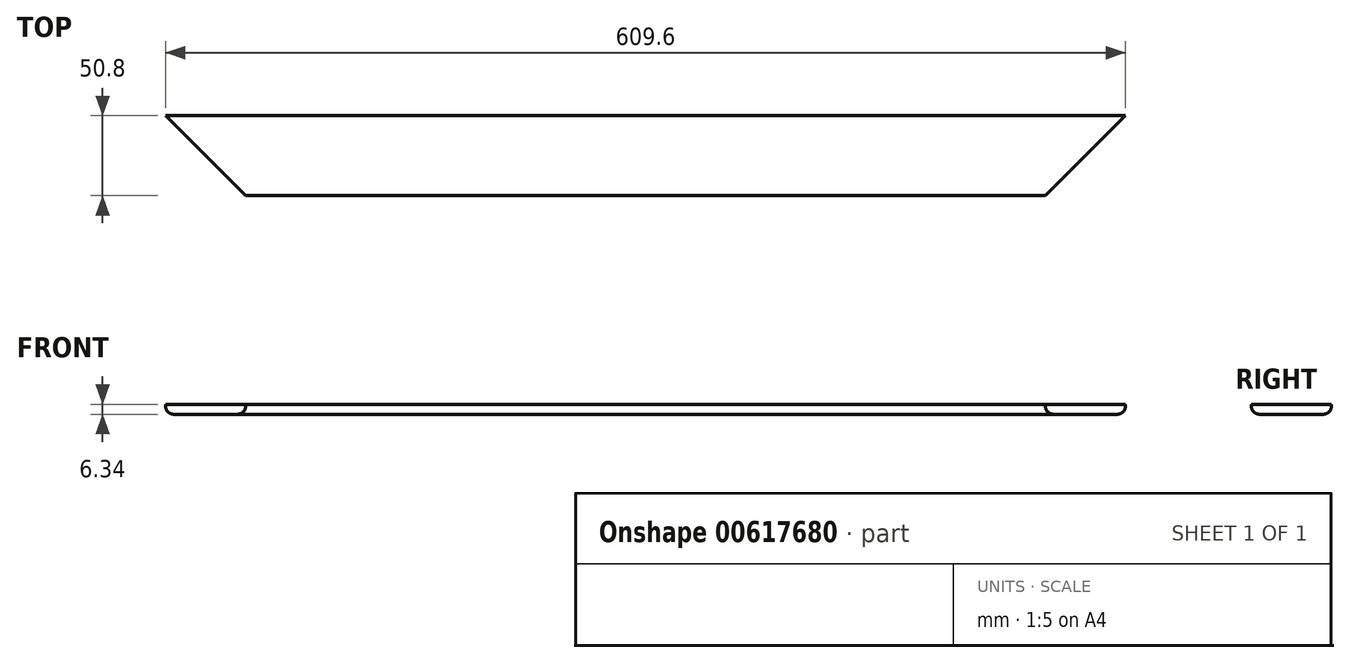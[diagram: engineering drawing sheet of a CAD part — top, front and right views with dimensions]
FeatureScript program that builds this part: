
annotation { "Feature Type Name" : "Feature", "Feature Type Description" : "" }
export const myFeature = defineFeature(function(context is Context, id is Id, definition is map)
    precondition{}
    {
        {
            var Q0;
            Q0=qCreatedBy(makeId("Top.planeOp"),FACE);
            var sketch = newSketch(context, id + "F0", { "sketchPlane" : qUnion([Q0])});
            skLineSegment(sketch, "E0", {"start": v(-305.19, 0) * mm, "end": v(304.41, 0) * mm});
            skLineSegment(sketch, "E1", {"start": v(-254.39, -50.8) * mm, "end": v(253.61, -50.8) * mm});
            skLineSegment(sketch, "E2", {"start": v(-305.19, 0) * mm, "end": v(-254.39, -50.8) * mm});
            skLineSegment(sketch, "E3", {"start": v(253.61, -50.8) * mm, "end": v(304.41, 0) * mm});
            skSolve(sketch);
        }
        {
            var Q0;
            Q0 = qSketchRegion(id + "F0", true);
            extrude(context, id + "F1", {"entities" : qUnion([Q0]), "endBound" : BoundingType.SYMMETRIC, "depth" : 6.35 * mm, "offsetDistance" : 25.4 * mm});
        }
        {
            var Q0;
            Q0=makeQuery(id+"F1.opExtrude","CAP_EDGE",EDGE,{"disambiguationData":[OSD([sQuery(id+"F0.wireOp",EDGE,"E1")])],"isStart":true});
            var Q1;
            Q1=makeQuery(id+"F1.opExtrude","CAP_EDGE",EDGE,{"disambiguationData":[OSD([sQuery(id+"F0.wireOp",EDGE,"E0")])],"isStart":true});
            fillet(context, id + "F2", {"entities" : qUnion([Q0, Q1]), "radius" : 5.08 * mm, "tangentPropagation" : true, "allowEdgeOverflow" : false});
        }
    });
